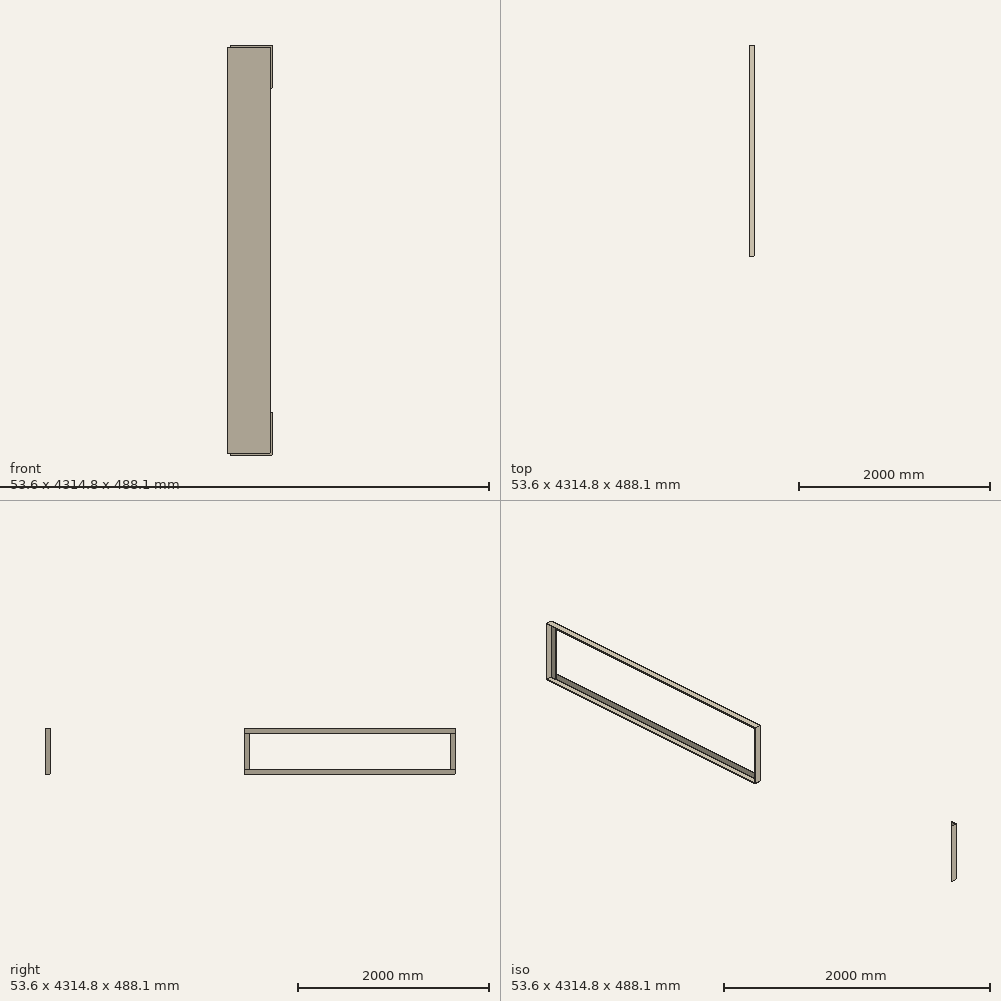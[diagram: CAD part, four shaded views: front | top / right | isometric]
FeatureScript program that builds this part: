
annotation { "Feature Type Name" : "Feature", "Feature Type Description" : "" }
export const myFeature = defineFeature(function(context is Context, id is Id, definition is map)
    precondition{}
    {
        {
            var Q0;
            Q0=qCreatedBy(makeId("Front.planeOp"),FACE);
            var sketch = newSketch(context, id + "F0", { "sketchPlane" : qUnion([Q0])});
            skLineSegment(sketch, "E0.bottom", {"start": v(0, 0) * mm, "end": v(-50.8, 0) * mm});
            skLineSegment(sketch, "E0.top", {"start": v(0, 50.8) * mm, "end": v(-2.77, 50.8) * mm});
            skLineSegment(sketch, "E0.left", {"start": v(0, 0) * mm, "end": v(0, 50.8) * mm});
            skLineSegment(sketch, "E0.right", {"start": v(-50.8, 0) * mm, "end": v(-50.8, 2.77) * mm});
            skLineSegment(sketch, "E1.top", {"start": v(-50.8, 2.77) * mm, "end": v(-2.77, 2.77) * mm});
            skLineSegment(sketch, "E1.right", {"start": v(-2.77, 50.8) * mm, "end": v(-2.77, 2.77) * mm});
            skSolve(sketch);
        }
        {
            var Q0;
            Q0 = qSketchRegion(id + "F0", true);
            extrude(context, id + "F1", {"entities" : qUnion([Q0]), "oppositeDirection" : true, "depth" : 2222.5 * mm});
        }
        {
            var Q0;
            Q0=makeQuery(id+"F1.opExtrude","SWEPT_FACE",FACE,{"disambiguationData":[OSD([sQuery(id+"F0.wireOp",EDGE,"E1.top")])]});
            var sketch = newSketch(context, id + "F2", { "sketchPlane" : qUnion([Q0])});
            skLineSegment(sketch, "E2.bottom", {"start": v(-2.77, 2222.5) * mm, "end": v(-53.57, 2222.5) * mm});
            skLineSegment(sketch, "E2.top", {"start": v(-2.77, 2171.7) * mm, "end": v(-5.54, 2171.7) * mm});
            skLineSegment(sketch, "E2.left", {"start": v(-2.77, 2222.5) * mm, "end": v(-2.77, 2171.7) * mm});
            skLineSegment(sketch, "E3.top", {"start": v(-53.57, 2219.73) * mm, "end": v(-5.54, 2219.73) * mm});
            skLineSegment(sketch, "E3.right", {"start": v(-5.54, 2171.7) * mm, "end": v(-5.54, 2219.73) * mm});
            skLineSegment(sketch, "E4", {"start": v(-53.57, 2222.5) * mm, "end": v(-53.57, 2219.73) * mm});
            skSolve(sketch);
        }
        {
            var Q0;
            Q0 = qSketchRegion(id + "F2", true);
            extrude(context, id + "F3", {"entities" : qUnion([Q0]), "depth" : 482.6 * mm});
        }
        {
            var Q0;
            Q0=qCreatedBy(makeId("Front.planeOp"),FACE);
            cPlane(context, id + "F4", {"entities" : qUnion([Q0]), "cplaneType" : CPlaneType.OFFSET, "offset" : 1111.25 * mm, "oppositeDirection" : true, "width" : 152.4 * mm, "height" : 152.4 * mm});
        }
        {
            var Q0;
            Q0=makeQuery(id+"F3.opExtrude","SWEPT_BODY",BODY,{"disambiguationData":[OSD([sQuery(id+"F2.wireOp",EDGE,"a5998e61-da0b-468a-a66f-6794bc91e38d0.MirrorCS"),sQuery(id+"F2.wireOp",EDGE,"a5998e61-da0b-468a-a66f-6794bc91e38d1.MirrorCS"),sQuery(id+"F2.wireOp",EDGE,"a5998e61-da0b-468a-a66f-6794bc91e38d2.MirrorCS"),sQuery(id+"F2.wireOp",EDGE,"a5998e61-da0b-468a-a66f-6794bc91e38d3.MirrorCS"),sQuery(id+"F2.wireOp",EDGE,"a5998e61-da0b-468a-a66f-6794bc91e38d4.MirrorCS"),sQuery(id+"F2.wireOp",EDGE,"a5998e61-da0b-468a-a66f-6794bc91e38d5.MirrorCS")])]});
            var Q1;
            Q1=makeQuery(id+"F3.opExtrude","SWEPT_BODY",BODY,{"disambiguationData":[OSD([sQuery(id+"F2.wireOp",EDGE,"E2.bottom"),sQuery(id+"F2.wireOp",EDGE,"E2.top"),sQuery(id+"F2.wireOp",EDGE,"E2.left"),sQuery(id+"F2.wireOp",EDGE,"E3.top"),sQuery(id+"F2.wireOp",EDGE,"E3.right"),sQuery(id+"F2.wireOp",EDGE,"E4")])]});
            var Q2;
            Q2=qCreatedBy(id+"F4.planeOp",FACE);
            mirror(context, id + "F5", {"entities" : qUnion([Q0, Q1]), "mirrorPlane" : qUnion([Q2])});
        }
        {
            var Q0;
            Q0=qCreatedBy(makeId("Top.planeOp"),FACE);
            cPlane(context, id + "F6", {"entities" : qUnion([Q0]), "cplaneType" : CPlaneType.OFFSET, "offset" : 244.07 * mm, "width" : 152.4 * mm, "height" : 152.4 * mm});
        }
        {
            var Q0;
            Q0=makeQuery(id+"F1.opExtrude","SWEPT_BODY",BODY,{"disambiguationData":[OSD([sQuery(id+"F0.wireOp",EDGE,"E0.bottom"),sQuery(id+"F0.wireOp",EDGE,"E0.top"),sQuery(id+"F0.wireOp",EDGE,"E0.left"),sQuery(id+"F0.wireOp",EDGE,"E0.right"),sQuery(id+"F0.wireOp",EDGE,"E1.top"),sQuery(id+"F0.wireOp",EDGE,"E1.right")])]});
            var Q1;
            Q1=qCreatedBy(id+"F6.planeOp",FACE);
            mirror(context, id + "F7", {"entities" : qUnion([Q0]), "mirrorPlane" : qUnion([Q1])});
        }
        {
            var Q0;
            Q0=qCreatedBy(makeId("Front.planeOp"),FACE);
            cPlane(context, id + "F8", {"entities" : qUnion([Q0]), "cplaneType" : CPlaneType.OFFSET, "offset" : ((87.5 * 3 / 4) - .5) * mm, "oppositeDirection" : true, "width" : 152.4 * mm, "height" : 152.4 * mm});
        }
        {
            var Q0;
            Q0=makeQuery(id+"F3.opExtrude","SWEPT_BODY",BODY,{"disambiguationData":[OSD([sQuery(id+"F2.wireOp",EDGE,"E2.bottom"),sQuery(id+"F2.wireOp",EDGE,"E2.top"),sQuery(id+"F2.wireOp",EDGE,"E2.left"),sQuery(id+"F2.wireOp",EDGE,"E3.top"),sQuery(id+"F2.wireOp",EDGE,"E3.right"),sQuery(id+"F2.wireOp",EDGE,"E4")])]});
            var Q1;
            Q1=qCreatedBy(id+"F8.planeOp",FACE);
            mirror(context, id + "F9", {"entities" : qUnion([Q0]), "mirrorPlane" : qUnion([Q1])});
        }
    });
